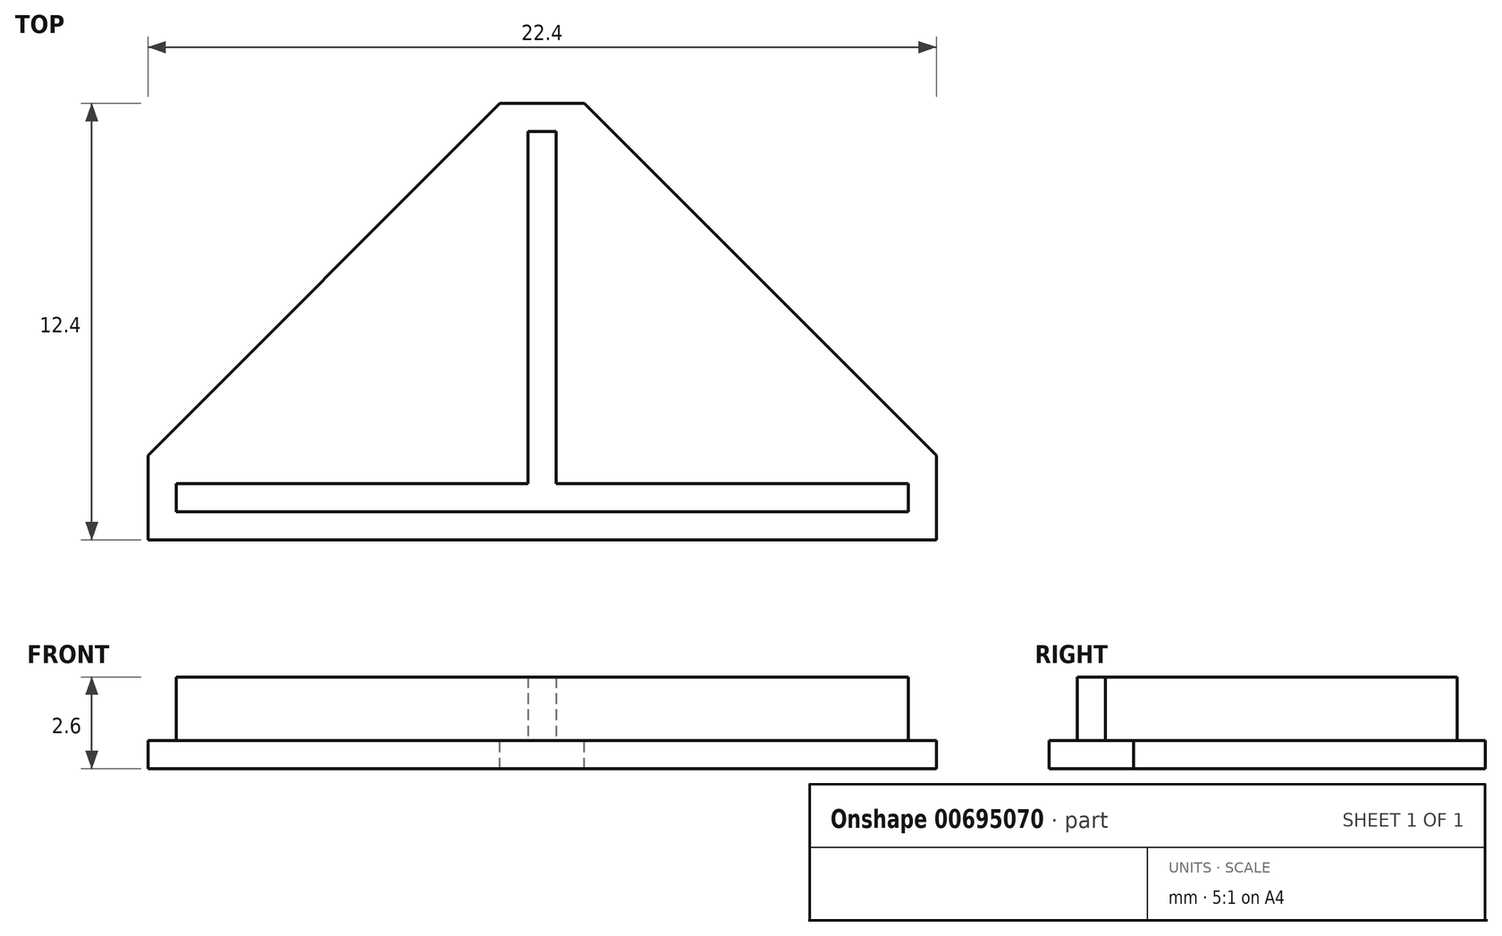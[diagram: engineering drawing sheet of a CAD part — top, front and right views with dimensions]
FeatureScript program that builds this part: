
annotation { "Feature Type Name" : "Feature", "Feature Type Description" : "" }
export const myFeature = defineFeature(function(context is Context, id is Id, definition is map)
    precondition{}
    {
        {
            var Q0;
            Q0=qCreatedBy(makeId("Top.planeOp"),FACE);
            var sketch = newSketch(context, id + "F0", { "sketchPlane" : qUnion([Q0])});
            skLineSegment(sketch, "E0", {"start": v(-0.4, 0.4) * mm, "end": v(-0.4, 10.4) * mm});
            skLineSegment(sketch, "E1", {"start": v(-0.4, 10.4) * mm, "end": v(0.4, 10.4) * mm});
            skLineSegment(sketch, "E2", {"start": v(0.4, 10.4) * mm, "end": v(0.4, 0.4) * mm});
            skLineSegment(sketch, "E3", {"start": v(0.4, 0.4) * mm, "end": v(10.4, 0.4) * mm});
            skLineSegment(sketch, "E4", {"start": v(10.4, 0.4) * mm, "end": v(10.4, -0.4) * mm});
            skLineSegment(sketch, "E5", {"start": v(10.4, -0.4) * mm, "end": v(0.4, -0.4) * mm});
            skLineSegment(sketch, "E6", {"start": v(0.4, -0.4) * mm, "end": v(0.4, -10.4) * mm});
            skLineSegment(sketch, "E7", {"start": v(0.4, -10.4) * mm, "end": v(-0.4, -10.4) * mm});
            skLineSegment(sketch, "E8", {"start": v(-0.4, -10.4) * mm, "end": v(-0.4, -0.4) * mm});
            skLineSegment(sketch, "E9", {"start": v(-0.4, -0.4) * mm, "end": v(-10.4, -0.4) * mm});
            skLineSegment(sketch, "E10", {"start": v(-10.4, -0.4) * mm, "end": v(-10.4, 0.4) * mm});
            skLineSegment(sketch, "E11", {"start": v(-10.4, 0.4) * mm, "end": v(-0.4, 0.4) * mm});
            skPoint(sketch, "E12", {"position": v(0, 10.4) * mm});
            skPoint(sketch, "E13", {"position": v(-10.4, 0) * mm});
            skLineSegment(sketch, "E14.0", {"start": v(-11.2, -1.2) * mm, "end": v(-11.2, 1.2) * mm});
            skLineSegment(sketch, "E14.1", {"start": v(1.2, 1.2) * mm, "end": v(11.2, 1.2) * mm});
            skLineSegment(sketch, "E14.2", {"start": v(1.2, 11.2) * mm, "end": v(1.2, 1.2) * mm});
            skLineSegment(sketch, "E14.3", {"start": v(-1.2, 11.2) * mm, "end": v(1.2, 11.2) * mm});
            skLineSegment(sketch, "E14.4", {"start": v(-1.2, 1.2) * mm, "end": v(-1.2, 11.2) * mm});
            skLineSegment(sketch, "E14.5", {"start": v(11.2, 1.2) * mm, "end": v(11.2, -1.2) * mm});
            skLineSegment(sketch, "E14.6", {"start": v(-11.2, 1.2) * mm, "end": v(-1.2, 1.2) * mm});
            skLineSegment(sketch, "E14.7", {"start": v(11.2, -1.2) * mm, "end": v(1.2, -1.2) * mm});
            skLineSegment(sketch, "E14.8", {"start": v(1.2, -1.2) * mm, "end": v(1.2, -11.2) * mm});
            skLineSegment(sketch, "E14.9", {"start": v(1.2, -11.2) * mm, "end": v(-1.2, -11.2) * mm});
            skLineSegment(sketch, "E14.10", {"start": v(-1.2, -11.2) * mm, "end": v(-1.2, -1.2) * mm});
            skLineSegment(sketch, "E14.11", {"start": v(-1.2, -1.2) * mm, "end": v(-11.2, -1.2) * mm});
            skLineSegment(sketch, "E15", {"start": v(-11.2, 1.2) * mm, "end": v(-1.2, 11.2) * mm});
            skLineSegment(sketch, "E16", {"start": v(1.2, 11.2) * mm, "end": v(11.2, 1.2) * mm});
            skLineSegment(sketch, "E17", {"start": v(11.2, -1.2) * mm, "end": v(1.2, -11.2) * mm});
            skLineSegment(sketch, "E18", {"start": v(-1.2, -11.2) * mm, "end": v(-11.2, -1.2) * mm});
            skLineSegment(sketch, "E19", {"start": v(-1.2, -1.2) * mm, "end": v(1.2, -1.2) * mm});
            skLineSegment(sketch, "E20", {"start": v(-0.4, -0.4) * mm, "end": v(0.4, -0.4) * mm});
            skSolve(sketch);
        }
        {
            var Q0;
            Q0=makeQuery(id+"F0.imprint","IMPRINT",FACE,{"disambiguationData":[TD([[makeQuery(id+"F0.imprint","IMPRINT",EDGE,{"derivedFrom":sQuery(id+"F0.wireOp",EDGE,"E0")}),-1.0]])]});
            extrude(context, id + "F1", {"entities" : qUnion([Q0]), "depth" : 1.8 * mm, "offsetDistance" : 25 * mm});
        }
        {
            var Q0;
            Q0=makeQuery(id+"F0.imprint","IMPRINT",FACE,{"disambiguationData":[TD([[makeQuery(id+"F0.imprint","IMPRINT",EDGE,{"derivedFrom":sQuery(id+"F0.wireOp",EDGE,"E14.4")}),1.0]])]});
            var Q1;
            Q1=makeQuery(id+"F0.imprint","IMPRINT",FACE,{"disambiguationData":[TD([[makeQuery(id+"F0.imprint","IMPRINT",EDGE,{"derivedFrom":sQuery(id+"F0.wireOp",EDGE,"E14.1")}),1.0]])]});
            var Q2;
            Q2=makeQuery(id+"F0.imprint","IMPRINT",FACE,{"disambiguationData":[TD([[makeQuery(id+"F0.imprint","IMPRINT",EDGE,{"derivedFrom":sQuery(id+"F0.wireOp",EDGE,"E0")}),1.0]])]});
            var Q3;
            Q3=makeQuery(id+"F1.opExtrude","CAP_FACE",FACE,{"disambiguationData":[OSD([sQuery(id+"F0.wireOp",EDGE,"E0"),sQuery(id+"F0.wireOp",EDGE,"E1"),sQuery(id+"F0.wireOp",EDGE,"E2"),sQuery(id+"F0.wireOp",EDGE,"E3"),sQuery(id+"F0.wireOp",EDGE,"E4"),sQuery(id+"F0.wireOp",EDGE,"E5"),sQuery(id+"F0.wireOp",EDGE,"E6"),sQuery(id+"F0.wireOp",EDGE,"E7"),sQuery(id+"F0.wireOp",EDGE,"E8"),sQuery(id+"F0.wireOp",EDGE,"E9"),sQuery(id+"F0.wireOp",EDGE,"E10"),sQuery(id+"F0.wireOp",EDGE,"E11")])],"isStart":false});
            var Q4;
            Q4=makeQuery(id+"F0.imprint","IMPRINT",FACE,{"disambiguationData":[TD([[makeQuery(id+"F0.imprint","IMPRINT",EDGE,{"derivedFrom":sQuery(id+"F0.wireOp",EDGE,"E0")}),-1.0]])]});
            var Q5;
            {var subQ0=sQuery(id+"F0.wireOp",EDGE,"E20");Q5=makeQuery(id+"F0.imprint","IMPRINT",FACE,{"disambiguationData":[TD([[makeQuery(id+"F0.imprint","IMPRINT",EDGE,{"derivedFrom":subQ0}),-1.0]])]});}
            extrude(context, id + "F2", {"entities" : qUnion([Q0, Q1, Q2, Q3, Q4, Q5]), "operationType" : NewBodyOperationType.ADD, "oppositeDirection" : true, "depth" : 0.8 * mm, "offsetDistance" : 25 * mm});
        }
    });
